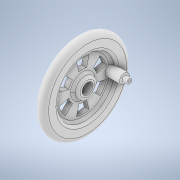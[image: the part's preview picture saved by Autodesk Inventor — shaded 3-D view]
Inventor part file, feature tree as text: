
AUTODESK INVENTOR PART (.ipt)
format: ipt  version: 2020 (Build 240168000, 168)  size: 286,208 bytes
history: native  units: in
note: dims shown in document units (in); Inventor stores cm internally (conversion verified against a paired STEP export)
features: sketch x4, extrude x4, revolve x1, fillet x1, pattern_circular x1, projected_geometry x1
ambient origin geometry x8: Origin, YZ Plane, XZ Plane, XY Plane, X Axis, Y Axis, Z Axis, Center Point
bodies: Solid1 (feature_tree)
feature tree (12):
  revolve  "Revolution1"  [1 undecoded]
  fillet  "Fillet1"  Radius=0.75in
  sketch  "Sketch2"  dims[d4=0.25in d5=0.125in]
  extrude  "Extrusion1"  Depth=0.125in
  extrude  "Extrusion2"  TaperAngle=90.0deg  [1 undecoded]
  extrude  "Extrusion3"  Depth=0.125in
  extrude  "Extrusion4"  Depth=0.125in
  pattern_circular  "Circular Pattern1"  [2 undecoded]
  sketch  "Sketch1"  dims[d0=0.14in d1=0.25in d2=0.75in]
  projected_geometry  "Projected Loop1"
  sketch  "Sketch3"  dims[d6=0.25in d7=90.0deg]
  sketch  "Sketch4"  dims[d8=0.063in d9=0.25in d10=0.125in d11=0.7in d12=0.375in d13=0.0in d14=0.5in d15=0.0in d16=0.0625in d17=0.25in d18=0.0in d19=0.74in d20=1.26in d21=15.0deg d22=15.0deg d23=0.25in d24=0.0in d25=2.3622in d26=360.0deg]
note: 4 required parameter values undecoded (feature->parameter linkage not recoverable at this tier; creation-order binding heuristic only, values carry confidence <= 0.55)